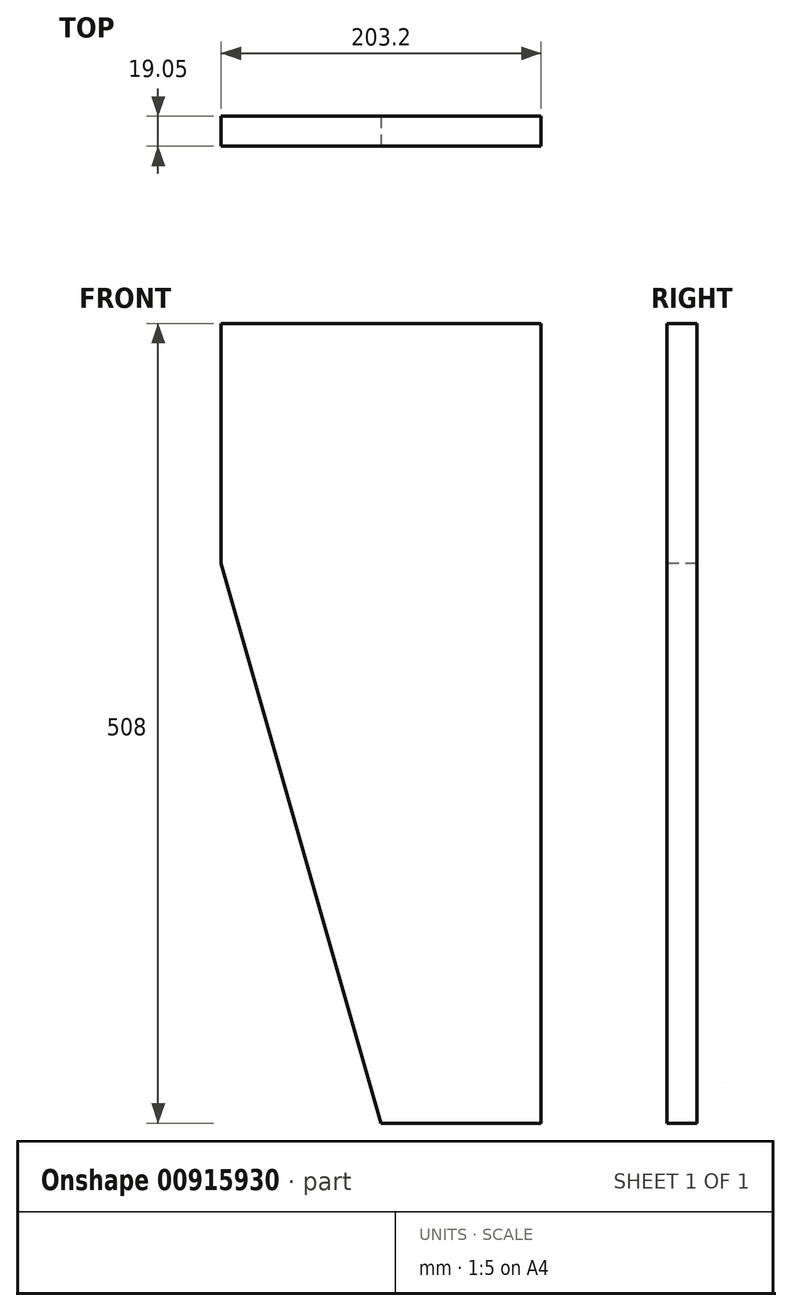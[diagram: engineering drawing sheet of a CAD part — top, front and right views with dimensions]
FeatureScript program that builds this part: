
annotation { "Feature Type Name" : "Feature", "Feature Type Description" : "" }
export const myFeature = defineFeature(function(context is Context, id is Id, definition is map)
    precondition{}
    {
        {
            var Q0;
            Q0=qCreatedBy(makeId("Front.planeOp"),FACE);
            var sketch = newSketch(context, id + "F0", { "sketchPlane" : qUnion([Q0])});
            skLineSegment(sketch, "E0.bottom", {"start": v(0, 0) * mm, "end": v(203.2, 0) * mm});
            skLineSegment(sketch, "E0.top", {"start": v(0, 508) * mm, "end": v(203.2, 508) * mm});
            skLineSegment(sketch, "E0.left", {"start": v(0, 0) * mm, "end": v(0, 508) * mm});
            skLineSegment(sketch, "E0.right", {"start": v(203.2, 0) * mm, "end": v(203.2, 508) * mm});
            skSolve(sketch);
        }
        {
            var Q0;
            Q0 = qSketchRegion(id + "F0", true);
            extrude(context, id + "F1", {"entities" : qUnion([Q0]), "depth" : 19.05 * mm, "offsetDistance" : 25.4 * mm});
        }
        {
            var Q0;
            Q0=makeQuery(id+"F1.opExtrude","CAP_FACE",FACE,{"disambiguationData":[OSD([sQuery(id+"F0.wireOp",EDGE,"E0.bottom"),sQuery(id+"F0.wireOp",EDGE,"E0.top"),sQuery(id+"F0.wireOp",EDGE,"E0.left"),sQuery(id+"F0.wireOp",EDGE,"E0.right")])],"isStart":false});
            var sketch = newSketch(context, id + "F2", { "sketchPlane" : qUnion([Q0])});
            skLineSegment(sketch, "E1", {"start": v(101.6, 0) * mm, "end": v(0, 0) * mm});
            skLineSegment(sketch, "E2", {"start": v(0, 0) * mm, "end": v(0, 355.6) * mm});
            skLineSegment(sketch, "E3", {"start": v(0, 355.6) * mm, "end": v(101.6, 0) * mm});
            skSolve(sketch);
        }
        {
            var Q0;
            Q0 = qSketchRegion(id + "F2", true);
            extrude(context, id + "F3", {"entities" : qUnion([Q0]), "operationType" : NewBodyOperationType.REMOVE, "endBound" : BoundingType.THROUGH_ALL, "oppositeDirection" : true, "depth" : 25.4 * mm, "offsetDistance" : 25.4 * mm});
        }
    });
